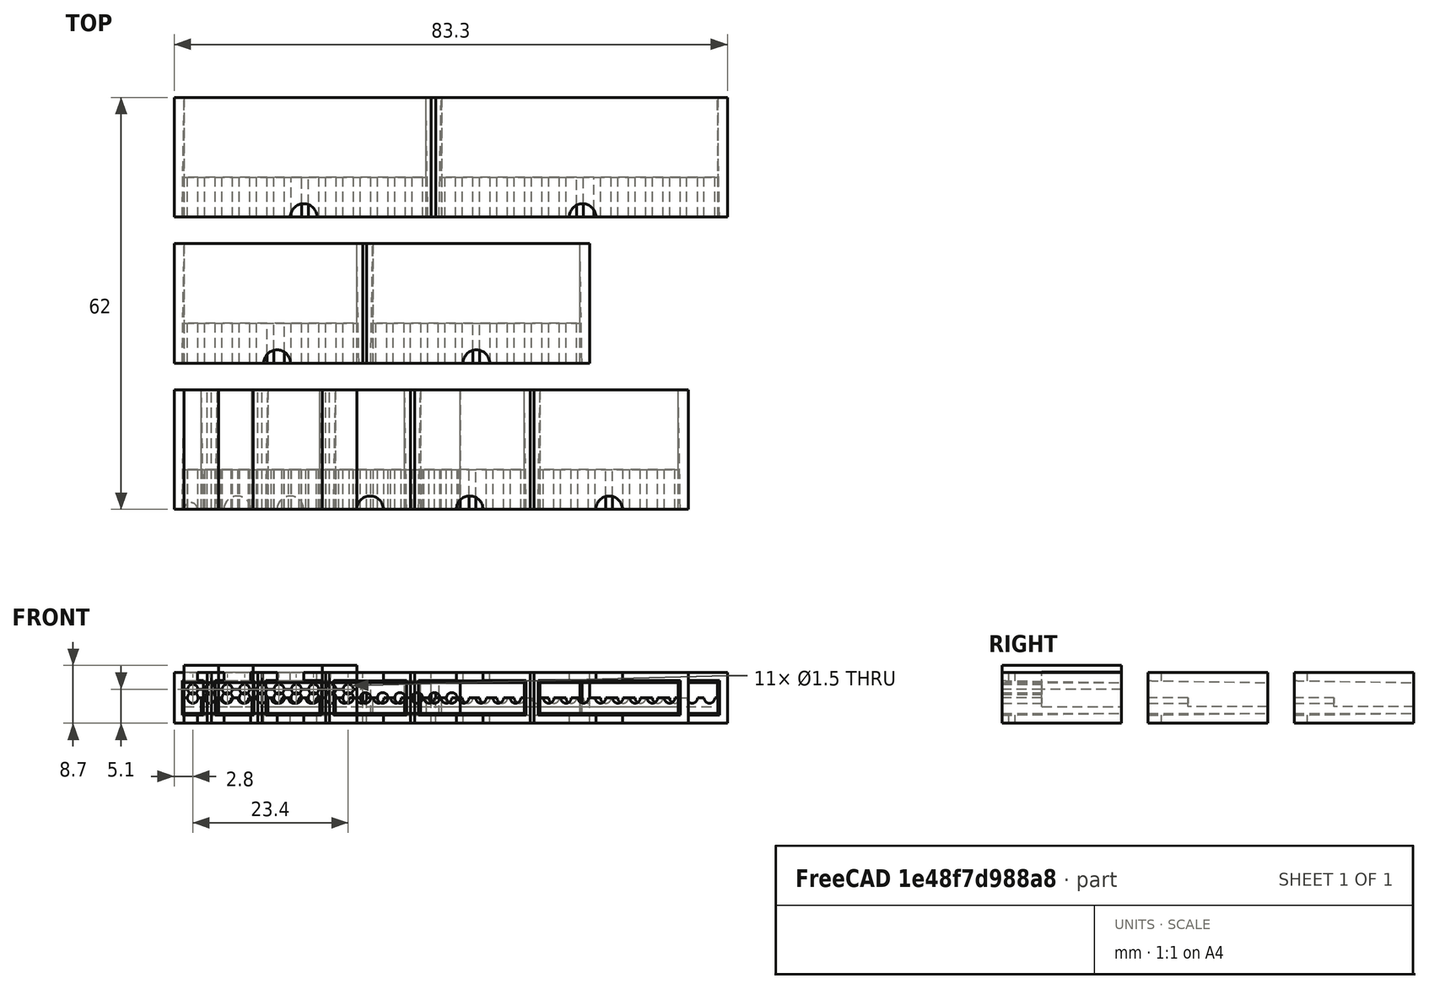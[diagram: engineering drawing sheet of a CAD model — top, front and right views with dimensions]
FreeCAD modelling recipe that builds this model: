
FCSTD DOCUMENT  (FreeCAD 0.18R4 (GitTag))
Label: dupont
License: CreativeCommons Attribution-ShareAlike
LicenseURL: http://creativecommons.org/licenses/by-sa/4.0/
objects: Part::Cut×57, Part::Box×47, Part::Cylinder×20, Part::FeaturePython×13, Part::Feature×10, Part::Wedge×10, App::DocumentObjectGroup×3, Part::Extrusion×1
note: 158 computed .brp shape members not serialized (recipe doc carries the construction recipe); baked Part::Feature solids carry a one-line shape summary decoded from their .brp

FEATURE [Part::Box] Box  label="cube_4_base"
  AttacherType = Attacher::AttachEngine3D
  Height = 7.2
  Length = 10.4
  Width = 18
FEATURE [Part::Box] Box001  label="cube_2_base"
  AttacherType = Attacher::AttachEngine3D
  Height = 7.2
  Length = 5.2
  Width = 18
FEATURE [Part::Box] Box002  label="cube_8_base"
  AttacherType = Attacher::AttachEngine3D
  Height = 7.2
  Length = 20.8
  Width = 18
FEATURE [Part::Box] Box003  label="cube_10_base"
  AttacherType = Attacher::AttachEngine3D
  Height = 7.2
  Length = 26
  Width = 18
FEATURE [Part::Cylinder] Cylinder
  Angle = 360
  AttacherType = Attacher::AttachEngine3D
  Height = 7
  Placement = pos=(1.3,-1,3.6) rot=(-1,0,0;1.5708rad)
  Radius = 0.75
FEATURE [Part::FeaturePython] Array  # Draft array (typed FeaturePython)
  Angle = 360
  ArrayType = 0
  Axis = (0,0,2.6)
  Base = -> Cylinder
  Center = (0,0,0)
  Fuse = false
  IntervalAxis = (0,0,0)
  IntervalX = (2.6,0,0)
  IntervalY = (0,1,0)
  IntervalZ = (0,0,1)
  NumberPolar = 1
  NumberX = 10
  NumberY = 2
  NumberZ = 1
FEATURE [Part::Cylinder] Cylinder001
  Angle = 360
  AttacherType = Attacher::AttachEngine3D
  Height = 7
  Placement = pos=(1.3,-1,3.6) rot=(-1,0,0;1.5708rad)
  Radius = 0.75
FEATURE [Part::FeaturePython] Array001  # Draft array (typed FeaturePython)
  Angle = 360
  ArrayType = 0
  Axis = (0,0,2.6)
  Base = -> Cylinder001
  Center = (0,0,0)
  Fuse = false
  IntervalAxis = (0,0,0)
  IntervalX = (2.6,0,0)
  IntervalY = (0,1,0)
  IntervalZ = (0,0,1)
  NumberPolar = 1
  NumberX = 2
  NumberY = 2
  NumberZ = 1
FEATURE [Part::Cylinder] Cylinder002
  Angle = 360
  AttacherType = Attacher::AttachEngine3D
  Height = 7
  Placement = pos=(1.3,-1,3.6) rot=(-1,0,0;1.5708rad)
  Radius = 0.75
FEATURE [Part::FeaturePython] Array002  # Draft array (typed FeaturePython)
  Angle = 360
  ArrayType = 0
  Axis = (0,0,2.6)
  Base = -> Cylinder002
  Center = (0,0,0)
  Fuse = false
  IntervalAxis = (0,0,0)
  IntervalX = (2.6,0,0)
  IntervalY = (0,1,0)
  IntervalZ = (0,0,1)
  NumberPolar = 1
  NumberX = 4
  NumberY = 2
  NumberZ = 1
FEATURE [Part::Cylinder] Cylinder003
  Angle = 360
  AttacherType = Attacher::AttachEngine3D
  Height = 7
  Placement = pos=(1.3,-1,3.6) rot=(-1,0,0;1.5708rad)
  Radius = 0.75
FEATURE [Part::FeaturePython] Array003  # Draft array (typed FeaturePython)
  Angle = 360
  ArrayType = 0
  Axis = (0,0,2.6)
  Base = -> Cylinder003
  Center = (0,0,0)
  Fuse = false
  IntervalAxis = (0,0,0)
  IntervalX = (2.6,0,0)
  IntervalY = (0,1,0)
  IntervalZ = (0,0,1)
  NumberPolar = 1
  NumberX = 8
  NumberY = 2
  NumberZ = 1
FEATURE [Part::Cut] Cut  label="cube_10_doble"
  Base = -> Box003
  Tool = -> Array
FEATURE [Part::Cut] Cut001  label="cube_2_doble"
  Base = -> Box001
  Tool = -> Array001
FEATURE [Part::Cut] Cut002  label="cube_4_doble"
  Base = -> Box
  Tool = -> Array002
FEATURE [Part::Cut] Cut003  label="cube_8_doble"
  Base = -> Box002
  Tool = -> Array003
FEATURE [Part::Box] Box004  label="cube_10_base001"
  AttacherType = Attacher::AttachEngine3D
  Height = 5.2
  Length = 26
  Placement = pos=(0,6,1) rot=(0,0,1;0rad)
  Width = 12
FEATURE [Part::Box] Box005  label="cube_10_base002"
  AttacherType = Attacher::AttachEngine3D
  Height = 5.2
  Length = 26
  Placement = pos=(0,6,1) rot=(0,0,1;0rad)
  Width = 12
FEATURE [Part::Box] Box006  label="cube_10_base003"
  AttacherType = Attacher::AttachEngine3D
  Height = 5.2
  Length = 26
  Placement = pos=(0,6,1) rot=(0,0,1;0rad)
  Width = 12
FEATURE [Part::Box] Box007  label="cube_10_base004"
  AttacherType = Attacher::AttachEngine3D
  Height = 5.2
  Length = 26
  Placement = pos=(0,6,1) rot=(0,0,1;0rad)
  Width = 12
FEATURE [Part::Cut] Cut004  label="bloque_10_doble_mal"
  Base = -> Cut
  Tool = -> Box004
FEATURE [Part::Cut] Cut005  label="bloque_8_doble"
  Base = -> Cut003
  Tool = -> Box005
FEATURE [Part::Cut] Cut006  label="bloque_4_doble"
  Base = -> Cut002
  Tool = -> Box007
FEATURE [Part::Cut] Cut007  label="bloque_2_doble"
  Base = -> Cut001
  Tool = -> Box006
FEATURE [Part::Box] Box008  label="cube_10_base005"
  AttacherType = Attacher::AttachEngine3D
  Height = 7.2
  Length = 26
  Width = 18
FEATURE [Part::Cylinder] Cylinder004
  Angle = 360
  AttacherType = Attacher::AttachEngine3D
  Height = 7
  Placement = pos=(1.3,-1,3.6) rot=(-1,0,0;1.5708rad)
  Radius = 0.75
FEATURE [Part::FeaturePython] Array004  # Draft array (typed FeaturePython)
  Angle = 360
  ArrayType = 0
  Axis = (0,0,2.6)
  Base = -> Cylinder004
  Center = (0,0,0)
  Fuse = false
  IntervalAxis = (0,0,0)
  IntervalX = (2.6,0,0)
  IntervalY = (0,1,0)
  IntervalZ = (0,0,1)
  NumberPolar = 1
  NumberX = 10
  NumberY = 2
  NumberZ = 1
FEATURE [Part::Box] Box009  label="cube_10_base006"
  AttacherType = Attacher::AttachEngine3D
  Height = 5.2
  Length = 26
  Placement = pos=(0,6,1) rot=(0,0,1;0rad)
  Width = 12
FEATURE [Part::Box] Box010  label="cube_8_base001"
  AttacherType = Attacher::AttachEngine3D
  Height = 7.2
  Length = 20.8
  Width = 18
FEATURE [Part::Cylinder] Cylinder005
  Angle = 360
  AttacherType = Attacher::AttachEngine3D
  Height = 7
  Placement = pos=(1.3,-1,3.6) rot=(-1,0,0;1.5708rad)
  Radius = 0.75
FEATURE [Part::FeaturePython] Array005  # Draft array (typed FeaturePython)
  Angle = 360
  ArrayType = 0
  Axis = (0,0,2.6)
  Base = -> Cylinder005
  Center = (0,0,0)
  Fuse = false
  IntervalAxis = (0,0,0)
  IntervalX = (2.6,0,0)
  IntervalY = (0,1,0)
  IntervalZ = (0,0,1)
  NumberPolar = 1
  NumberX = 8
  NumberY = 2
  NumberZ = 1
FEATURE [Part::Cut] Cut011  label="cube_8_doble001"
  Base = -> Box010
  Tool = -> Array005
FEATURE [Part::Box] Box011  label="cube_10_base007"
  AttacherType = Attacher::AttachEngine3D
  Height = 5.2
  Length = 26
  Placement = pos=(0,6,1) rot=(0,0,1;0rad)
  Width = 12
FEATURE [Part::Cut] Cut010  label="bloque_8_doble001"
  Base = -> Cut011
  Tool = -> Box011
FEATURE [Part::Cylinder] Cylinder006
  Angle = 360
  AttacherType = Attacher::AttachEngine3D
  Height = 7
  Placement = pos=(1.3,-1,3.6) rot=(-1,0,0;1.5708rad)
  Radius = 0.75
FEATURE [Part::Box] Box012  label="cube_4_base001"
  AttacherType = Attacher::AttachEngine3D
  Height = 7.2
  Length = 10.4
  Width = 18
FEATURE [Part::FeaturePython] Array006  # Draft array (typed FeaturePython)
  Angle = 360
  ArrayType = 0
  Axis = (0,0,2.6)
  Base = -> Cylinder006
  Center = (0,0,0)
  Fuse = false
  IntervalAxis = (0,0,0)
  IntervalX = (2.6,0,0)
  IntervalY = (0,1,0)
  IntervalZ = (0,0,1)
  NumberPolar = 1
  NumberX = 4
  NumberY = 2
  NumberZ = 1
FEATURE [Part::Cut] Cut013  label="cube_4_doble001"
  Base = -> Box012
  Tool = -> Array006
FEATURE [Part::Box] Box013  label="cube_10_base008"
  AttacherType = Attacher::AttachEngine3D
  Height = 5.2
  Length = 26
  Placement = pos=(0,6,1) rot=(0,0,1;0rad)
  Width = 12
FEATURE [Part::Cut] Cut012  label="bloque_4_doble001"
  Base = -> Cut013
  Tool = -> Box013
FEATURE [Part::Cylinder] Cylinder007
  Angle = 360
  AttacherType = Attacher::AttachEngine3D
  Height = 7
  Placement = pos=(1.3,-1,3.6) rot=(-1,0,0;1.5708rad)
  Radius = 0.75
FEATURE [Part::Box] Box014  label="cube_2_base001"
  AttacherType = Attacher::AttachEngine3D
  Height = 7.2
  Length = 5.2
  Width = 18
FEATURE [Part::FeaturePython] Array007  # Draft array (typed FeaturePython)
  Angle = 360
  ArrayType = 0
  Axis = (0,0,2.6)
  Base = -> Cylinder007
  Center = (0,0,0)
  Fuse = false
  IntervalAxis = (0,0,0)
  IntervalX = (2.6,0,0)
  IntervalY = (0,1,0)
  IntervalZ = (0,0,1)
  NumberPolar = 1
  NumberX = 2
  NumberY = 2
  NumberZ = 1
FEATURE [Part::Cut] Cut015  label="cube_2_doble001"
  Base = -> Box014
  Tool = -> Array007
FEATURE [Part::Box] Box015  label="cube_10_base009"
  AttacherType = Attacher::AttachEngine3D
  Height = 5.2
  Length = 26
  Placement = pos=(0,6,1) rot=(0,0,1;0rad)
  Width = 12
FEATURE [Part::Cut] Cut014  label="bloque_2_doble001"
  Base = -> Cut015
  Tool = -> Box015
FEATURE [Part::Box] Box016  label="cortador"
  AttacherType = Attacher::AttachEngine3D
  Height = 9.2
  Length = 30
  Placement = pos=(-1,-2,-5.6) rot=(0,0,1;0rad)
  Width = 20
FEATURE [Part::Box] Box018  label="cortador002"
  AttacherType = Attacher::AttachEngine3D
  Height = 9.2
  Length = 30
  Placement = pos=(-1,-2,-5.6) rot=(0,0,1;0rad)
  Width = 20
FEATURE [Part::Box] Box019  label="cortador003"
  AttacherType = Attacher::AttachEngine3D
  Height = 9.2
  Length = 30
  Placement = pos=(-1,-2,-5.6) rot=(0,0,1;0rad)
  Width = 20
FEATURE [Part::Box] Box020  label="cortador004"
  AttacherType = Attacher::AttachEngine3D
  Height = 9.2
  Length = 30
  Placement = pos=(-1,-1,-5.6) rot=(0,0,1;0rad)
  Width = 20
FEATURE [Part::Box] Box021  label="cortador005"
  AttacherType = Attacher::AttachEngine3D
  Height = 9.2
  Length = 30
  Placement = pos=(-1,-2,3.6) rot=(0,0,1;0rad)
  Width = 20
FEATURE [Part::Box] Box022  label="cortador006"
  AttacherType = Attacher::AttachEngine3D
  Height = 9.2
  Length = 30
  Placement = pos=(-1,-2,3.6) rot=(0,0,1;0rad)
  Width = 20
FEATURE [Part::Box] Box023  label="cortador007"
  AttacherType = Attacher::AttachEngine3D
  Height = 9.2
  Length = 30
  Placement = pos=(-1,-2,3.6) rot=(0,0,1;0rad)
  Width = 20
FEATURE [Part::Cut] Cut016  label="bloque2_arriba"
  Base = -> Cut014
  Tool = -> Box016
FEATURE [Part::Cut] Cut017  label="bloque2_abajo"
  Base = -> Cut007
  Tool = -> Box021
FEATURE [Part::Cut] Cut018  label="bloque4_arriba"
  Base = -> Cut012
  Tool = -> Box018
FEATURE [Part::Cut] Cut019  label="bloque4_abajo"
  Base = -> Cut006
  Tool = -> Box023
FEATURE [Part::Cut] Cut020  label="bloque8_arriba"
  Base = -> Cut005
  Tool = -> Box019
FEATURE [Part::Cut] Cut021  label="bloque8_abajo"
  Base = -> Cut010
  Tool = -> Box022
FEATURE [Part::Cut] Cut022
  Base = -> Box008
  Tool = -> Box009
FEATURE [Part::Cut] Cut023  label="bloque_10_doble"
  Base = -> Cut022
  Tool = -> Array004
FEATURE [Part::Box] Box024  label="cube_10_base010"
  AttacherType = Attacher::AttachEngine3D
  Height = 7.2
  Length = 26
  Width = 18
FEATURE [Part::Box] Box025  label="cube_10_base011"
  AttacherType = Attacher::AttachEngine3D
  Height = 5.2
  Length = 26
  Placement = pos=(0,6,1) rot=(0,0,1;0rad)
  Width = 12
FEATURE [Part::Cut] Cut025
  Base = -> Box024
  Tool = -> Box025
FEATURE [Part::Cylinder] Cylinder008
  Angle = 360
  AttacherType = Attacher::AttachEngine3D
  Height = 7
  Placement = pos=(1.3,-1,3.6) rot=(-1,0,0;1.5708rad)
  Radius = 0.75
FEATURE [Part::FeaturePython] Array008  # Draft array (typed FeaturePython)
  Angle = 360
  ArrayType = 0
  Axis = (0,0,2.6)
  Base = -> Cylinder008
  Center = (0,0,0)
  Fuse = false
  IntervalAxis = (0,0,0)
  IntervalX = (2.6,0,0)
  IntervalY = (0,1,0)
  IntervalZ = (0,0,1)
  NumberPolar = 1
  NumberX = 10
  NumberY = 2
  NumberZ = 1
FEATURE [Part::Cut] Cut024  label="bloque_10_doble001"
  Base = -> Cut025
  Tool = -> Array008
FEATURE [Part::Box] Box026  label="cortador008"
  AttacherType = Attacher::AttachEngine3D
  Height = 9.2
  Length = 30
  Placement = pos=(-1,-1,3.6) rot=(0,0,1;0rad)
  Width = 20
FEATURE [Part::Cut] Cut026  label="bloque10_arriba"
  Base = -> Cut023
  Tool = -> Box020
FEATURE [Part::Cut] Cut027  label="bloque_10_Arriba"
  Base = -> Cut024
  Tool = -> Box026
FEATURE [Part::Box] Box027  label="cube_10_base012"
  AttacherType = Attacher::AttachEngine3D
  Height = 4.6
  Length = 41.6
  Width = 18
FEATURE [Part::Box] Box028  label="cube_10_base013"
  AttacherType = Attacher::AttachEngine3D
  Height = 2.6
  Length = 43.6
  Placement = pos=(-1,6,1) rot=(0,0,1;0rad)
  Width = 14
FEATURE [Part::Cut] Cut029
  Base = -> Box027
  Tool = -> Box028
FEATURE [Part::Cylinder] Cylinder009
  Angle = 360
  AttacherType = Attacher::AttachEngine3D
  Height = 7
  Placement = pos=(1.3,-1,3.6) rot=(-1,0,0;1.5708rad)
  Radius = 0.8
FEATURE [Part::FeaturePython] Array009  # Draft array (typed FeaturePython)
  Angle = 360
  ArrayType = 0
  Axis = (0,0,2.6)
  Base = -> Cylinder009
  Center = (0,0,0)
  Fuse = false
  IntervalAxis = (0,0,0)
  IntervalX = (2.6,0,0)
  IntervalY = (0,1,0)
  IntervalZ = (0,0,1)
  NumberPolar = 1
  NumberX = 16
  NumberY = 2
  NumberZ = 1
  Placement = pos=(0,0,-1.3) rot=(0,0,1;0rad)
FEATURE [Part::Cut] Cut030  label="bloque_entero_16"
  Base = -> Cut029
  Tool = -> Array009
FEATURE [Part::Extrusion] Extrude  label="plano_de_corte"
  Dir = (1,-2e-16,3e-16)
  DirMode = 2
  FaceMakerClass = Part::FaceMakerBullseye
  LengthFwd = 50
  LengthRev = 0
  Placement = pos=(-5,0,0) rot=(0,0,1;0rad)
  Solid = false
  Symmetric = false
FEATURE [Part::FeaturePython] Slice  # WARN: FeaturePython — macro-defined, semantics opaque (R4)
  Base = -> Cut030
  Mode = 1
  Tolerance = 0
  Tools = -> [Extrude]
FEATURE [Part::FeaturePython] Slice_child0  label="bloque_16_arriba"  # WARN: FeaturePython — macro-defined, semantics opaque (R4)
  Base = -> Slice
  FilterType = 1
  Invert = false
  OverrideMaxVal = 0
  WindowFrom = 80
  WindowTo = 100
  items = 0
FEATURE [Part::FeaturePython] Slice_child1  label="bloque_16_abajo"  # WARN: FeaturePython — macro-defined, semantics opaque (R4)
  Base = -> Slice
  FilterType = 1
  Invert = false
  OverrideMaxVal = 0
  WindowFrom = 80
  WindowTo = 100
  items = 1
FEATURE [App::DocumentObjectGroup] GrExplode_Slice  label="bloque_16_sliced"
  Group = -> [Slice_child0,Slice_child1]
FEATURE [Part::Feature] Slice_child1001  label="simple_bloque_16"
  Placement = pos=(38.8,44,0) rot=(0,0,1;0rad)
  shape: bbox 41.6 x 18 x 2.3 mm, 40 faces (baked)
FEATURE [Part::Feature] Slice_child1002  label="simple_bloque_14_1"
  shape: bbox 41.6 x 18 x 2.3 mm, 40 faces (baked)
FEATURE [Part::Feature] Slice_child1003  label="simple_bloque_12_1"
  shape: bbox 41.6 x 18 x 2.3 mm, 40 faces (baked)
FEATURE [Part::Feature] Slice_child1004  label="simple_bloque_10_1"
  shape: bbox 41.6 x 18 x 2.3 mm, 40 faces (baked)
FEATURE [Part::Feature] Slice_child1005  label="simple_bloque_08_1"
  shape: bbox 41.6 x 18 x 2.3 mm, 40 faces (baked)
FEATURE [Part::Feature] Slice_child1006  label="simple_bloque_06_1"
  shape: bbox 41.6 x 18 x 2.3 mm, 40 faces (baked)
FEATURE [Part::Feature] Slice_child1007  label="simple_bloque_04_1"
  shape: bbox 41.6 x 18 x 2.3 mm, 40 faces (baked)
FEATURE [Part::Feature] Slice_child1008  label="simple_bloque_03_1"
  shape: bbox 41.6 x 18 x 2.3 mm, 40 faces (baked)
FEATURE [Part::Feature] Slice_child1009  label="simple_bloque_02_1"
  shape: bbox 41.6 x 18 x 2.3 mm, 40 faces (baked)
FEATURE [Part::Feature] Slice_child1010  label="simple_bloque_01_1"
  shape: bbox 41.6 x 18 x 2.3 mm, 40 faces (baked)
FEATURE [Part::Box] Box029  label="Cube"
  AttacherType = Attacher::AttachEngine3D
  Height = 10
  Length = 45
  Placement = pos=(36.4,-1,-1) rot=(0,0,1;0rad)
  Width = 20
FEATURE [Part::Box] Box030  label="Cube001"
  AttacherType = Attacher::AttachEngine3D
  Height = 10
  Length = 45
  Placement = pos=(31.2,-1,-1) rot=(0,0,1;0rad)
  Width = 20
FEATURE [Part::Cut] Cut031  label="simple_bloque_14"
  Base = -> Slice_child1002
  Placement = pos=(0,44,0) rot=(0,0,1;0rad)
  Tool = -> Box029
FEATURE [Part::Cut] Cut032  label="simple_bloque_12"
  Base = -> Slice_child1003
  Placement = pos=(28.4,22,0) rot=(0,0,1;0rad)
  Tool = -> Box030
FEATURE [Part::Box] Box031  label="Cube002"
  AttacherType = Attacher::AttachEngine3D
  Height = 10
  Length = 45
  Placement = pos=(26,-1,-1) rot=(0,0,1;0rad)
  Width = 20
FEATURE [Part::Box] Box032  label="Cube003"
  AttacherType = Attacher::AttachEngine3D
  Height = 10
  Length = 45
  Placement = pos=(20.8,-1,-1) rot=(0,0,1;0rad)
  Width = 20
FEATURE [Part::Cut] Cut033  label="simple_bloque_10"
  Base = -> Slice_child1004
  Placement = pos=(0,22,0) rot=(0,0,1;0rad)
  Tool = -> Box031
FEATURE [Part::Box] Box033  label="Cube004"
  AttacherType = Attacher::AttachEngine3D
  Height = 10
  Length = 45
  Placement = pos=(15.6,-1,-1) rot=(0,0,1;0rad)
  Width = 20
FEATURE [Part::Cut] Cut034  label="simple_bloque_08"
  Base = -> Slice_child1005
  Placement = pos=(53.6,0,0) rot=(0,0,1;0rad)
  Tool = -> Box032
FEATURE [Part::Box] Box034  label="Cube005"
  AttacherType = Attacher::AttachEngine3D
  Height = 10
  Length = 45
  Placement = pos=(10.4,-1,-1) rot=(0,0,1;0rad)
  Width = 20
FEATURE [Part::Cut] Cut035  label="simple_bloque_06"
  Base = -> Slice_child1006
  Placement = pos=(35.6,0,0) rot=(0,0,1;0rad)
  Tool = -> Box033
FEATURE [Part::Box] Box035  label="Cube006"
  AttacherType = Attacher::AttachEngine3D
  Height = 10
  Length = 45
  Placement = pos=(7.8,-1,-1) rot=(0,0,1;0rad)
  Width = 20
FEATURE [Part::Box] Box036  label="Cube007"
  AttacherType = Attacher::AttachEngine3D
  Height = 10
  Length = 45
  Placement = pos=(5.2,-1,-1) rot=(0,0,1;0rad)
  Width = 20
FEATURE [Part::Box] Box037  label="Cube008"
  AttacherType = Attacher::AttachEngine3D
  Height = 10
  Length = 45
  Placement = pos=(2.6,-1,-1) rot=(0,0,1;0rad)
  Width = 20
FEATURE [Part::Cut] Cut036  label="simple_bloque_04"
  Base = -> Slice_child1007
  Placement = pos=(22.8,0,0) rot=(0,0,1;0rad)
  Tool = -> Box034
FEATURE [Part::Cut] Cut037  label="simple_bloque_03"
  Base = -> Slice_child1008
  Placement = pos=(12.6,0,0) rot=(0,0,1;0rad)
  Tool = -> Box035
FEATURE [Part::Cut] Cut038  label="simple_bloque_02"
  Base = -> Slice_child1009
  Placement = pos=(5,0,0) rot=(0,0,1;0rad)
  Tool = -> Box036
FEATURE [Part::Cut] Cut039  label="simple_bloque_01"
  Base = -> Slice_child1010
  Tool = -> Box037
FEATURE [App::DocumentObjectGroup] Group  label="version1_bad_sizes"
  Group = -> [Cut004,Cut016,Cut017,Cut018,Cut019,Cut020,Cut021,Cut026,Cut027]
FEATURE [App::DocumentObjectGroup] Group001  label="version2_to_test"
  Group = -> [Slice_child1001,Cut031,Cut032,Cut033,Cut034,Cut035,Cut036,Cut037,Cut038,Cut039]
FEATURE [Part::Box] Box038  label="CubeX1"
  AttacherType = Attacher::AttachEngine3D
  Height = 7.6
  Length = 5.6
  Placement = pos=(-1.5,0,-1.5) rot=(0,0,1;0rad)
  Width = 18
FEATURE [Part::Wedge] Wedge  label="WedgeX1"
  AttacherType = Attacher::AttachEngine3D
  Placement = pos=(-0.3,0,-0.3) rot=(0,0,1;0rad)
  X2max = 2.9
  X2min = 0.3
  Xmax = 3.2
  Xmin = 0
  Ymax = 18
  Ymin = 0
  Z2max = 4.9
  Z2min = 0.3
  Zmax = 5.2
  Zmin = 0
FEATURE [Part::Box] Box039  label="CubeX002"
  AttacherType = Attacher::AttachEngine3D
  Height = 7.6
  Length = 8.2
  Placement = pos=(-1.5,0,-1.5) rot=(0,0,1;0rad)
  Width = 18
FEATURE [Part::Wedge] Wedge001  label="WedgeX002"
  AttacherType = Attacher::AttachEngine3D
  Placement = pos=(-0.3,0,-0.3) rot=(0,0,1;0rad)
  X2max = 5.5
  X2min = 0.3
  Xmax = 5.8
  Xmin = 0
  Ymax = 18
  Ymin = 0
  Z2max = 4.9
  Z2min = 0.3
  Zmax = 5.2
  Zmin = 0
FEATURE [Part::Cut] Cut040  label="cierreX1"
  Base = -> Box038
  Tool = -> Wedge
FEATURE [Part::Box] Box040  label="CubeX003"
  AttacherType = Attacher::AttachEngine3D
  Height = 7.6
  Length = 10.8
  Placement = pos=(-1.5,0,-1.5) rot=(0,0,1;0rad)
  Width = 18
FEATURE [Part::Wedge] Wedge002  label="WedgeX003"
  AttacherType = Attacher::AttachEngine3D
  Placement = pos=(-0.3,0,-0.3) rot=(0,0,1;0rad)
  X2max = 8.1
  X2min = 0.3
  Xmax = 8.4
  Xmin = 0
  Ymax = 18
  Ymin = 0
  Z2max = 4.9
  Z2min = 0.3
  Zmax = 5.2
  Zmin = 0
FEATURE [Part::Cut] Cut041  label="cierreX2"
  Base = -> Box039
  Placement = pos=(5,0,0) rot=(0,0,1;0rad)
  Tool = -> Wedge001
FEATURE [Part::Cut] Cut042  label="cierreX3"
  Base = -> Box040
  Placement = pos=(12.6,0,0) rot=(0,0,1;0rad)
  Tool = -> Wedge002
FEATURE [Part::Box] Box041  label="CubeX004"
  AttacherType = Attacher::AttachEngine3D
  Height = 7.6
  Length = 13.4
  Placement = pos=(-1.5,0,-1.5) rot=(0,0,1;0rad)
  Width = 18
FEATURE [Part::Wedge] Wedge003  label="WedgeX004"
  AttacherType = Attacher::AttachEngine3D
  Placement = pos=(-0.3,0,-0.3) rot=(0,0,1;0rad)
  X2max = 10.7
  X2min = 0.3
  Xmax = 11
  Xmin = 0
  Ymax = 18
  Ymin = 0
  Z2max = 4.9
  Z2min = 0.3
  Zmax = 5.2
  Zmin = 0
FEATURE [Part::Cut] Cut043  label="cierreX4"
  Base = -> Box041
  Placement = pos=(22.8,0,0) rot=(0,0,1;0rad)
  Tool = -> Wedge003
FEATURE [Part::Box] Box043  label="CubeX006"
  AttacherType = Attacher::AttachEngine3D
  Height = 7.6
  Length = 18.6
  Placement = pos=(-1.5,0,-1.5) rot=(0,0,1;0rad)
  Width = 18
FEATURE [Part::Wedge] Wedge005  label="WedgeX006"
  AttacherType = Attacher::AttachEngine3D
  Placement = pos=(-0.3,0,-0.3) rot=(0,0,1;0rad)
  X2max = 15.9
  X2min = 0.3
  Xmax = 16.2
  Xmin = 0
  Ymax = 18
  Ymin = 0
  Z2max = 4.9
  Z2min = 0.3
  Zmax = 5.2
  Zmin = 0
FEATURE [Part::Cut] Cut044  label="cierreX6"
  Base = -> Box043
  Placement = pos=(35.6,0,0) rot=(0,0,1;0rad)
  Tool = -> Wedge005
FEATURE [Part::Box] Box045  label="CubeX008"
  AttacherType = Attacher::AttachEngine3D
  Height = 7.6
  Length = 23.8
  Placement = pos=(-1.5,0,-1.5) rot=(0,0,1;0rad)
  Width = 18
FEATURE [Part::Wedge] Wedge007  label="WedgeX008"
  AttacherType = Attacher::AttachEngine3D
  Placement = pos=(-0.3,0,-0.3) rot=(0,0,1;0rad)
  X2max = 21.1
  X2min = 0.3
  Xmax = 21.4
  Xmin = 0
  Ymax = 18
  Ymin = 0
  Z2max = 4.9
  Z2min = 0.3
  Zmax = 5.2
  Zmin = 0
FEATURE [Part::Cut] Cut045  label="cierreX8"
  Base = -> Box045
  Placement = pos=(53.6,0,0) rot=(0,0,1;0rad)
  Tool = -> Wedge007
FEATURE [Part::Box] Box047  label="CubeX010"
  AttacherType = Attacher::AttachEngine3D
  Height = 7.6
  Length = 29
  Placement = pos=(-1.5,0,-1.5) rot=(0,0,1;0rad)
  Width = 18
FEATURE [Part::Wedge] Wedge009  label="WedgeX010"
  AttacherType = Attacher::AttachEngine3D
  Placement = pos=(-0.3,0,-0.3) rot=(0,0,1;0rad)
  X2max = 26.3
  X2min = 0.3
  Xmax = 26.6
  Xmin = 0
  Ymax = 18
  Ymin = 0
  Z2max = 4.9
  Z2min = 0.3
  Zmax = 5.2
  Zmin = 0
FEATURE [Part::Cut] Cut046  label="cierreX10"
  Base = -> Box047
  Placement = pos=(0,22,0) rot=(0,0,1;0rad)
  Tool = -> Wedge009
FEATURE [Part::Box] Box049  label="CubeX012"
  AttacherType = Attacher::AttachEngine3D
  Height = 7.6
  Length = 34.2
  Placement = pos=(-1.5,0,-1.5) rot=(0,0,1;0rad)
  Width = 18
FEATURE [Part::Wedge] Wedge011  label="WedgeX012"
  AttacherType = Attacher::AttachEngine3D
  Placement = pos=(-0.3,0,-0.3) rot=(0,0,1;0rad)
  X2max = 31.5
  X2min = 0.3
  Xmax = 31.8
  Xmin = 0
  Ymax = 18
  Ymin = 0
  Z2max = 4.9
  Z2min = 0.3
  Zmax = 5.2
  Zmin = 0
FEATURE [Part::Cut] Cut047  label="cierrex12"
  Base = -> Box049
  Placement = pos=(28.4,22,0) rot=(0,0,1;0rad)
  Tool = -> Wedge011
FEATURE [Part::Box] Box051  label="CubeX014"
  AttacherType = Attacher::AttachEngine3D
  Height = 7.6
  Length = 39.4
  Placement = pos=(-1.5,0,-1.5) rot=(0,0,1;0rad)
  Width = 18
FEATURE [Part::Wedge] Wedge013  label="WedgeX014"
  AttacherType = Attacher::AttachEngine3D
  Placement = pos=(-0.3,0,-0.3) rot=(0,0,1;0rad)
  X2max = 36.7
  X2min = 0.3
  Xmax = 37
  Xmin = 0
  Ymax = 18
  Ymin = 0
  Z2max = 4.9
  Z2min = 0.3
  Zmax = 5.2
  Zmin = 0
FEATURE [Part::Cut] Cut048  label="cierreX14"
  Base = -> Box051
  Placement = pos=(0,44,0) rot=(0,0,1;0rad)
  Tool = -> Wedge013
FEATURE [Part::Box] Box053  label="CubeX016"
  AttacherType = Attacher::AttachEngine3D
  Height = 7.6
  Length = 44.6
  Placement = pos=(-1.5,0,-1.5) rot=(0,0,1;0rad)
  Width = 18
FEATURE [Part::Wedge] Wedge015  label="WedgeX016"
  AttacherType = Attacher::AttachEngine3D
  Placement = pos=(-0.3,0,-0.3) rot=(0,0,1;0rad)
  X2max = 41.9
  X2min = 0.3
  Xmax = 42.2
  Xmin = 0
  Ymax = 18
  Ymin = 0
  Z2max = 4.9
  Z2min = 0.3
  Zmax = 5.2
  Zmin = 0
FEATURE [Part::Cut] Cut049  label="cierreX16"
  Base = -> Box053
  Placement = pos=(38.7,44,0) rot=(0,0,1;0rad)
  Tool = -> Wedge015
FEATURE [Part::Cylinder] Cylinder010
  Angle = 360
  AttacherType = Attacher::AttachEngine3D
  Height = 10
  Placement = pos=(1,0,-3) rot=(0,0,1;0rad)
  Radius = 1
FEATURE [Part::Cylinder] Cylinder011
  Angle = 360
  AttacherType = Attacher::AttachEngine3D
  Height = 10
  Placement = pos=(44,22,-3) rot=(0,0,1;0rad)
  Radius = 2
FEATURE [Part::Cylinder] Cylinder012
  Angle = 360
  AttacherType = Attacher::AttachEngine3D
  Height = 10
  Placement = pos=(18,44,-3) rot=(0,0,1;0rad)
  Radius = 2
FEATURE [Part::Cylinder] Cylinder013
  Angle = 360
  AttacherType = Attacher::AttachEngine3D
  Height = 10
  Placement = pos=(60,44,-3) rot=(0,0,1;0rad)
  Radius = 2
FEATURE [Part::Cylinder] Cylinder014
  Angle = 360
  AttacherType = Attacher::AttachEngine3D
  Height = 10
  Placement = pos=(14,22,-3) rot=(0,0,1;0rad)
  Radius = 2
FEATURE [Part::Cylinder] Cylinder015
  Angle = 360
  AttacherType = Attacher::AttachEngine3D
  Height = 10
  Placement = pos=(8,0,-3) rot=(0,0,1;0rad)
  Radius = 2
FEATURE [Part::Cylinder] Cylinder016
  Angle = 360
  AttacherType = Attacher::AttachEngine3D
  Height = 10
  Placement = pos=(16,0,-3) rot=(0,0,1;0rad)
  Radius = 2
FEATURE [Part::Cylinder] Cylinder017
  Angle = 360
  AttacherType = Attacher::AttachEngine3D
  Height = 10
  Placement = pos=(28,0,-3) rot=(0,0,1;0rad)
  Radius = 2
FEATURE [Part::Cylinder] Cylinder018
  Angle = 360
  AttacherType = Attacher::AttachEngine3D
  Height = 10
  Placement = pos=(43,0,-3) rot=(0,0,1;0rad)
  Radius = 2
FEATURE [Part::Cylinder] Cylinder019
  Angle = 360
  AttacherType = Attacher::AttachEngine3D
  Height = 10
  Placement = pos=(64,0,-3) rot=(0,0,1;0rad)
  Radius = 2
FEATURE [Part::Cut] Cut050  label="cierreX16_v2"
  Base = -> Cut049
  Tool = -> Cylinder013
FEATURE [Part::Cut] Cut051  label="cierreX14_v2"
  Base = -> Cut048
  Tool = -> Cylinder012
FEATURE [Part::Cut] Cut052  label="cierreX10_v2"
  Base = -> Cut046
  Tool = -> Cylinder014
FEATURE [Part::Cut] Cut053  label="cierrex12_v2"
  Base = -> Cut047
  Tool = -> Cylinder011
FEATURE [Part::Cut] Cut054  label="cierreX1_v2"
  Base = -> Cut040
  Tool = -> Cylinder010
FEATURE [Part::Cut] Cut055  label="cierreX2_v2"
  Base = -> Cut041
  Tool = -> Cylinder015
FEATURE [Part::Cut] Cut056  label="cierreX3_v2"
  Base = -> Cut042
  Tool = -> Cylinder016
FEATURE [Part::Cut] Cut057  label="cierreX4_v2"
  Base = -> Cut043
  Tool = -> Cylinder017
FEATURE [Part::Cut] Cut058  label="cierreX6_v2"
  Base = -> Cut044
  Tool = -> Cylinder018
FEATURE [Part::Cut] Cut059  label="cierreX8_v2"
  Base = -> Cut045
  Tool = -> Cylinder019
